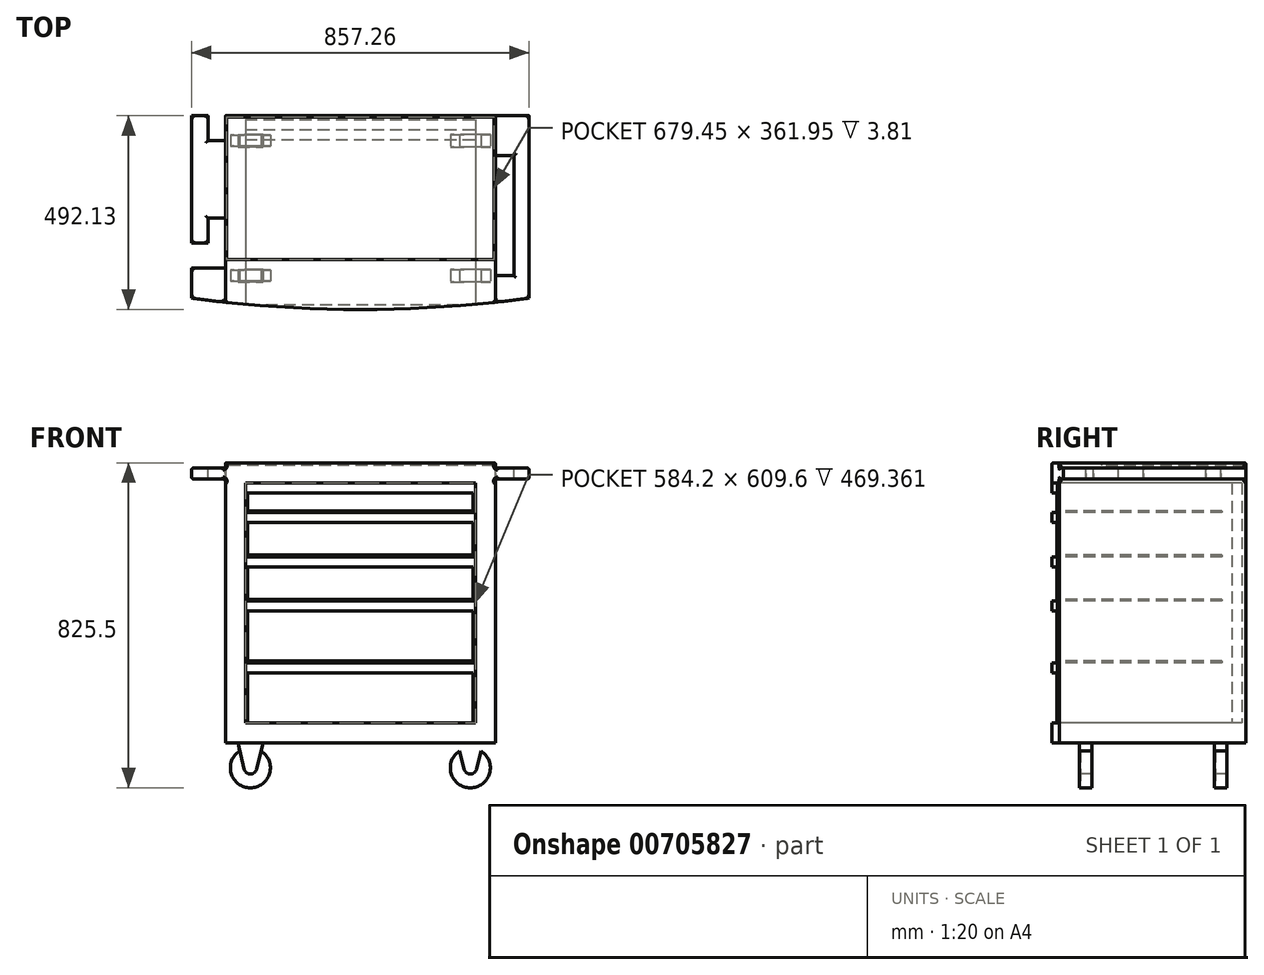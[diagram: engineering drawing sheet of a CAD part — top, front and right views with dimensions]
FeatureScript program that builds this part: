
annotation { "Feature Type Name" : "Feature", "Feature Type Description" : "" }
export const myFeature = defineFeature(function(context is Context, id is Id, definition is map)
    precondition{}
    {
        {
            var Q0;
            Q0=qCreatedBy(makeId("Front.planeOp"),FACE);
            var sketch = newSketch(context, id + "F0", { "sketchPlane" : qUnion([Q0])});
            skLineSegment(sketch, "E0", {"start": v(0, 0) * mm, "end": v(685.8, 0) * mm});
            skLineSegment(sketch, "E1", {"start": v(685.8, 0) * mm, "end": v(685.8, 669.92) * mm});
            skLineSegment(sketch, "E2", {"start": v(685.8, 669.93) * mm, "end": v(771.52, 669.93) * mm});
            skLineSegment(sketch, "E3", {"start": v(771.52, 669.93) * mm, "end": v(771.52, 711.2) * mm});
            skLineSegment(sketch, "E4", {"start": v(771.52, 711.2) * mm, "end": v(-85.72, 711.2) * mm});
            skLineSegment(sketch, "E5", {"start": v(-85.73, 711.2) * mm, "end": v(-85.73, 669.93) * mm});
            skLineSegment(sketch, "E6", {"start": v(-85.72, 669.93) * mm, "end": v(0, 669.93) * mm});
            skLineSegment(sketch, "E7", {"start": v(0, 669.92) * mm, "end": v(0, 0) * mm});
            skPoint(sketch, "E8", {"position": v(342.9, 711.2) * mm});
            skPoint(sketch, "E9", {"position": v(342.9, 0) * mm});
            skLineSegment(sketch, "E10.bottom", {"start": v(50.8, 660.4) * mm, "end": v(635, 660.4) * mm});
            skLineSegment(sketch, "E10.top", {"start": v(50.8, 50.8) * mm, "end": v(635, 50.8) * mm});
            skLineSegment(sketch, "E10.left", {"start": v(50.8, 660.4) * mm, "end": v(50.8, 50.8) * mm});
            skLineSegment(sketch, "E10.right", {"start": v(635, 660.4) * mm, "end": v(635, 50.8) * mm});
            skLineSegment(sketch, "E11", {"start": v(50.8, 203.2) * mm, "end": v(635, 203.2) * mm});
            skLineSegment(sketch, "E12", {"start": v(50.8, 360.04) * mm, "end": v(635, 360.05) * mm});
            skLineSegment(sketch, "E13", {"start": v(50.8, 472.44) * mm, "end": v(635, 472.44) * mm});
            skLineSegment(sketch, "E14", {"start": v(50.8, 584.83) * mm, "end": v(635, 584.84) * mm});
            skLineSegment(sketch, "E15", {"start": v(50.8, 207.64) * mm, "end": v(635, 207.65) * mm});
            skLineSegment(sketch, "E16", {"start": v(50.8, 364.49) * mm, "end": v(635, 364.5) * mm});
            skLineSegment(sketch, "E17", {"start": v(50.8, 476.88) * mm, "end": v(635, 476.89) * mm});
            skLineSegment(sketch, "E18", {"start": v(50.8, 589.28) * mm, "end": v(635, 589.28) * mm});
            skLineSegment(sketch, "E19", {"start": v(50.8, 635) * mm, "end": v(635, 635) * mm});
            skLineSegment(sketch, "E20", {"start": v(50.8, 559.43) * mm, "end": v(635, 559.44) * mm});
            skLineSegment(sketch, "E21", {"start": v(50.8, 447.04) * mm, "end": v(635, 447.04) * mm});
            skLineSegment(sketch, "E22", {"start": v(50.8, 334.64) * mm, "end": v(635, 334.65) * mm});
            skLineSegment(sketch, "E23", {"start": v(50.8, 177.8) * mm, "end": v(635, 177.8) * mm});
            skSolve(sketch);
        }
        {
            var Q0;
            Q0=makeQuery(id+"F0.imprint","IMPRINT",FACE,{"disambiguationData":[TD([[makeQuery(id+"F0.imprint","IMPRINT",EDGE,{"derivedFrom":sQuery(id+"F0.wireOp",EDGE,"E0")}),1.0]])]});
            var Q1;
            {var subQ0=sQuery(id+"F0.wireOp",EDGE,"E10.top");Q1=makeQuery(id+"F0.imprint","IMPRINT",FACE,{"disambiguationData":[TD([[makeQuery(id+"F0.imprint","IMPRINT",EDGE,{"derivedFrom":subQ0}),1.0]])]});}
            var Q2;
            {var subQ0=sQuery(id+"F0.wireOp",EDGE,"E11");Q2=makeQuery(id+"F0.imprint","IMPRINT",FACE,{"disambiguationData":[TD([[makeQuery(id+"F0.imprint","IMPRINT",EDGE,{"derivedFrom":subQ0}),-1.0]])]});}
            var Q3;
            {var subQ0=sQuery(id+"F0.wireOp",EDGE,"E11");Q3=makeQuery(id+"F0.imprint","IMPRINT",FACE,{"disambiguationData":[TD([[makeQuery(id+"F0.imprint","IMPRINT",EDGE,{"derivedFrom":subQ0}),1.0]])]});}
            var Q4;
            {var subQ0=sQuery(id+"F0.wireOp",EDGE,"E15");Q4=makeQuery(id+"F0.imprint","IMPRINT",FACE,{"disambiguationData":[TD([[makeQuery(id+"F0.imprint","IMPRINT",EDGE,{"derivedFrom":subQ0}),1.0]])]});}
            var Q5;
            {var subQ0=sQuery(id+"F0.wireOp",EDGE,"E12");Q5=makeQuery(id+"F0.imprint","IMPRINT",FACE,{"disambiguationData":[TD([[makeQuery(id+"F0.imprint","IMPRINT",EDGE,{"derivedFrom":subQ0}),-1.0]])]});}
            var Q6;
            {var subQ0=sQuery(id+"F0.wireOp",EDGE,"E12");Q6=makeQuery(id+"F0.imprint","IMPRINT",FACE,{"disambiguationData":[TD([[makeQuery(id+"F0.imprint","IMPRINT",EDGE,{"derivedFrom":subQ0}),1.0]])]});}
            var Q7;
            {var subQ0=sQuery(id+"F0.wireOp",EDGE,"E16");Q7=makeQuery(id+"F0.imprint","IMPRINT",FACE,{"disambiguationData":[TD([[makeQuery(id+"F0.imprint","IMPRINT",EDGE,{"derivedFrom":subQ0}),1.0]])]});}
            var Q8;
            {var subQ0=sQuery(id+"F0.wireOp",EDGE,"E13");Q8=makeQuery(id+"F0.imprint","IMPRINT",FACE,{"disambiguationData":[TD([[makeQuery(id+"F0.imprint","IMPRINT",EDGE,{"derivedFrom":subQ0}),-1.0]])]});}
            var Q9;
            {var subQ0=sQuery(id+"F0.wireOp",EDGE,"E13");Q9=makeQuery(id+"F0.imprint","IMPRINT",FACE,{"disambiguationData":[TD([[makeQuery(id+"F0.imprint","IMPRINT",EDGE,{"derivedFrom":subQ0}),1.0]])]});}
            var Q10;
            {var subQ0=sQuery(id+"F0.wireOp",EDGE,"E17");Q10=makeQuery(id+"F0.imprint","IMPRINT",FACE,{"disambiguationData":[TD([[makeQuery(id+"F0.imprint","IMPRINT",EDGE,{"derivedFrom":subQ0}),1.0]])]});}
            var Q11;
            {var subQ0=sQuery(id+"F0.wireOp",EDGE,"E14");Q11=makeQuery(id+"F0.imprint","IMPRINT",FACE,{"disambiguationData":[TD([[makeQuery(id+"F0.imprint","IMPRINT",EDGE,{"derivedFrom":subQ0}),-1.0]])]});}
            var Q12;
            {var subQ0=sQuery(id+"F0.wireOp",EDGE,"E14");Q12=makeQuery(id+"F0.imprint","IMPRINT",FACE,{"disambiguationData":[TD([[makeQuery(id+"F0.imprint","IMPRINT",EDGE,{"derivedFrom":subQ0}),1.0]])]});}
            var Q13;
            {var subQ0=sQuery(id+"F0.wireOp",EDGE,"E18");Q13=makeQuery(id+"F0.imprint","IMPRINT",FACE,{"disambiguationData":[TD([[makeQuery(id+"F0.imprint","IMPRINT",EDGE,{"derivedFrom":subQ0}),1.0]])]});}
            var Q14;
            {var subQ0=sQuery(id+"F0.wireOp",EDGE,"E10.bottom");Q14=makeQuery(id+"F0.imprint","IMPRINT",FACE,{"disambiguationData":[TD([[makeQuery(id+"F0.imprint","IMPRINT",EDGE,{"derivedFrom":subQ0}),-1.0]])]});}
            extrude(context, id + "F1", {"entities" : qUnion([Q0, Q1, Q2, Q3, Q4, Q5, Q6, Q7, Q8, Q9, Q10, Q11, Q12, Q13, Q14]), "oppositeDirection" : true, "depth" : 492.12 * mm, "offsetDistance" : 25.4 * mm});
        }
        {
            var Q0;
            {var subQ0=sQuery(id+"F0.wireOp",EDGE,"E10.bottom");Q0=makeQuery(id+"F0.imprint","IMPRINT",FACE,{"disambiguationData":[TD([[makeQuery(id+"F0.imprint","IMPRINT",EDGE,{"derivedFrom":subQ0}),-1.0]])]});}
            var Q1;
            {var subQ0=sQuery(id+"F0.wireOp",EDGE,"E18");Q1=makeQuery(id+"F0.imprint","IMPRINT",FACE,{"disambiguationData":[TD([[makeQuery(id+"F0.imprint","IMPRINT",EDGE,{"derivedFrom":subQ0}),1.0]])]});}
            var Q2;
            {var subQ0=sQuery(id+"F0.wireOp",EDGE,"E14");Q2=makeQuery(id+"F0.imprint","IMPRINT",FACE,{"disambiguationData":[TD([[makeQuery(id+"F0.imprint","IMPRINT",EDGE,{"derivedFrom":subQ0}),1.0]])]});}
            var Q3;
            {var subQ0=sQuery(id+"F0.wireOp",EDGE,"E14");Q3=makeQuery(id+"F0.imprint","IMPRINT",FACE,{"disambiguationData":[TD([[makeQuery(id+"F0.imprint","IMPRINT",EDGE,{"derivedFrom":subQ0}),-1.0]])]});}
            var Q4;
            {var subQ0=sQuery(id+"F0.wireOp",EDGE,"E17");Q4=makeQuery(id+"F0.imprint","IMPRINT",FACE,{"disambiguationData":[TD([[makeQuery(id+"F0.imprint","IMPRINT",EDGE,{"derivedFrom":subQ0}),1.0]])]});}
            var Q5;
            {var subQ0=sQuery(id+"F0.wireOp",EDGE,"E13");Q5=makeQuery(id+"F0.imprint","IMPRINT",FACE,{"disambiguationData":[TD([[makeQuery(id+"F0.imprint","IMPRINT",EDGE,{"derivedFrom":subQ0}),1.0]])]});}
            var Q6;
            {var subQ0=sQuery(id+"F0.wireOp",EDGE,"E13");Q6=makeQuery(id+"F0.imprint","IMPRINT",FACE,{"disambiguationData":[TD([[makeQuery(id+"F0.imprint","IMPRINT",EDGE,{"derivedFrom":subQ0}),-1.0]])]});}
            var Q7;
            {var subQ0=sQuery(id+"F0.wireOp",EDGE,"E16");Q7=makeQuery(id+"F0.imprint","IMPRINT",FACE,{"disambiguationData":[TD([[makeQuery(id+"F0.imprint","IMPRINT",EDGE,{"derivedFrom":subQ0}),1.0]])]});}
            var Q8;
            {var subQ0=sQuery(id+"F0.wireOp",EDGE,"E12");Q8=makeQuery(id+"F0.imprint","IMPRINT",FACE,{"disambiguationData":[TD([[makeQuery(id+"F0.imprint","IMPRINT",EDGE,{"derivedFrom":subQ0}),1.0]])]});}
            var Q9;
            {var subQ0=sQuery(id+"F0.wireOp",EDGE,"E12");Q9=makeQuery(id+"F0.imprint","IMPRINT",FACE,{"disambiguationData":[TD([[makeQuery(id+"F0.imprint","IMPRINT",EDGE,{"derivedFrom":subQ0}),-1.0]])]});}
            var Q10;
            {var subQ0=sQuery(id+"F0.wireOp",EDGE,"E15");Q10=makeQuery(id+"F0.imprint","IMPRINT",FACE,{"disambiguationData":[TD([[makeQuery(id+"F0.imprint","IMPRINT",EDGE,{"derivedFrom":subQ0}),1.0]])]});}
            var Q11;
            {var subQ0=sQuery(id+"F0.wireOp",EDGE,"E11");Q11=makeQuery(id+"F0.imprint","IMPRINT",FACE,{"disambiguationData":[TD([[makeQuery(id+"F0.imprint","IMPRINT",EDGE,{"derivedFrom":subQ0}),1.0]])]});}
            var Q12;
            {var subQ0=sQuery(id+"F0.wireOp",EDGE,"E11");Q12=makeQuery(id+"F0.imprint","IMPRINT",FACE,{"disambiguationData":[TD([[makeQuery(id+"F0.imprint","IMPRINT",EDGE,{"derivedFrom":subQ0}),-1.0]])]});}
            var Q13;
            {var subQ0=sQuery(id+"F0.wireOp",EDGE,"E10.top");Q13=makeQuery(id+"F0.imprint","IMPRINT",FACE,{"disambiguationData":[TD([[makeQuery(id+"F0.imprint","IMPRINT",EDGE,{"derivedFrom":subQ0}),1.0]])]});}
            extrude(context, id + "F2", {"entities" : qUnion([Q0, Q1, Q2, Q3, Q4, Q5, Q6, Q7, Q8, Q9, Q10, Q11, Q12, Q13]), "operationType" : NewBodyOperationType.REMOVE, "oppositeDirection" : true, "depth" : 482.6 * mm, "offsetDistance" : 25.4 * mm});
        }
        {
            var Q0;
            {var subQ0=sQuery(id+"F0.wireOp",EDGE,"E10.bottom");Q0=makeQuery(id+"F0.imprint","IMPRINT",FACE,{"disambiguationData":[TD([[makeQuery(id+"F0.imprint","IMPRINT",EDGE,{"derivedFrom":subQ0}),-1.0]])]});}
            var Q1;
            {var subQ0=sQuery(id+"F0.wireOp",EDGE,"E18");Q1=makeQuery(id+"F0.imprint","IMPRINT",FACE,{"disambiguationData":[TD([[makeQuery(id+"F0.imprint","IMPRINT",EDGE,{"derivedFrom":subQ0}),1.0]])]});}
            var Q2;
            {var subQ0=sQuery(id+"F0.wireOp",EDGE,"E14");Q2=makeQuery(id+"F0.imprint","IMPRINT",FACE,{"disambiguationData":[TD([[makeQuery(id+"F0.imprint","IMPRINT",EDGE,{"derivedFrom":subQ0}),-1.0]])]});}
            var Q3;
            {var subQ0=sQuery(id+"F0.wireOp",EDGE,"E17");Q3=makeQuery(id+"F0.imprint","IMPRINT",FACE,{"disambiguationData":[TD([[makeQuery(id+"F0.imprint","IMPRINT",EDGE,{"derivedFrom":subQ0}),1.0]])]});}
            var Q4;
            {var subQ0=sQuery(id+"F0.wireOp",EDGE,"E13");Q4=makeQuery(id+"F0.imprint","IMPRINT",FACE,{"disambiguationData":[TD([[makeQuery(id+"F0.imprint","IMPRINT",EDGE,{"derivedFrom":subQ0}),-1.0]])]});}
            var Q5;
            {var subQ0=sQuery(id+"F0.wireOp",EDGE,"E16");Q5=makeQuery(id+"F0.imprint","IMPRINT",FACE,{"disambiguationData":[TD([[makeQuery(id+"F0.imprint","IMPRINT",EDGE,{"derivedFrom":subQ0}),1.0]])]});}
            var Q6;
            {var subQ0=sQuery(id+"F0.wireOp",EDGE,"E12");Q6=makeQuery(id+"F0.imprint","IMPRINT",FACE,{"disambiguationData":[TD([[makeQuery(id+"F0.imprint","IMPRINT",EDGE,{"derivedFrom":subQ0}),-1.0]])]});}
            var Q7;
            {var subQ0=sQuery(id+"F0.wireOp",EDGE,"E15");Q7=makeQuery(id+"F0.imprint","IMPRINT",FACE,{"disambiguationData":[TD([[makeQuery(id+"F0.imprint","IMPRINT",EDGE,{"derivedFrom":subQ0}),1.0]])]});}
            var Q8;
            {var subQ0=sQuery(id+"F0.wireOp",EDGE,"E11");Q8=makeQuery(id+"F0.imprint","IMPRINT",FACE,{"disambiguationData":[TD([[makeQuery(id+"F0.imprint","IMPRINT",EDGE,{"derivedFrom":subQ0}),-1.0]])]});}
            var Q9;
            {var subQ0=sQuery(id+"F0.wireOp",EDGE,"E10.top");Q9=makeQuery(id+"F0.imprint","IMPRINT",FACE,{"disambiguationData":[TD([[makeQuery(id+"F0.imprint","IMPRINT",EDGE,{"derivedFrom":subQ0}),1.0]])]});}
            var Q10;
            {var subQ0=sQuery(id+"F0.wireOp",EDGE,"E11");Q10=makeQuery(id+"F0.imprint","IMPRINT",FACE,{"disambiguationData":[TD([[makeQuery(id+"F0.imprint","IMPRINT",EDGE,{"derivedFrom":subQ0}),1.0]])]});}
            var Q11;
            {var subQ0=sQuery(id+"F0.wireOp",EDGE,"E12");Q11=makeQuery(id+"F0.imprint","IMPRINT",FACE,{"disambiguationData":[TD([[makeQuery(id+"F0.imprint","IMPRINT",EDGE,{"derivedFrom":subQ0}),1.0]])]});}
            var Q12;
            {var subQ0=sQuery(id+"F0.wireOp",EDGE,"E13");Q12=makeQuery(id+"F0.imprint","IMPRINT",FACE,{"disambiguationData":[TD([[makeQuery(id+"F0.imprint","IMPRINT",EDGE,{"derivedFrom":subQ0}),1.0]])]});}
            var Q13;
            {var subQ0=sQuery(id+"F0.wireOp",EDGE,"E14");Q13=makeQuery(id+"F0.imprint","IMPRINT",FACE,{"disambiguationData":[TD([[makeQuery(id+"F0.imprint","IMPRINT",EDGE,{"derivedFrom":subQ0}),1.0]])]});}
            extrude(context, id + "F3", {"entities" : qUnion([Q0, Q1, Q2, Q3, Q4, Q5, Q6, Q7, Q8, Q9, Q10, Q11, Q12, Q13]), "oppositeDirection" : true, "depth" : 457.2 * mm, "offsetDistance" : 25.4 * mm});
        }
        {
            var Q0;
            {var subQ0=sQuery(id+"F0.wireOp",EDGE,"E18");Q0=makeQuery(id+"F0.imprint","IMPRINT",FACE,{"disambiguationData":[TD([[makeQuery(id+"F0.imprint","IMPRINT",EDGE,{"derivedFrom":subQ0}),1.0]])]});}
            var Q1;
            {var subQ0=sQuery(id+"F0.wireOp",EDGE,"E17");Q1=makeQuery(id+"F0.imprint","IMPRINT",FACE,{"disambiguationData":[TD([[makeQuery(id+"F0.imprint","IMPRINT",EDGE,{"derivedFrom":subQ0}),1.0]])]});}
            var Q2;
            {var subQ0=sQuery(id+"F0.wireOp",EDGE,"E16");Q2=makeQuery(id+"F0.imprint","IMPRINT",FACE,{"disambiguationData":[TD([[makeQuery(id+"F0.imprint","IMPRINT",EDGE,{"derivedFrom":subQ0}),1.0]])]});}
            var Q3;
            {var subQ0=sQuery(id+"F0.wireOp",EDGE,"E15");Q3=makeQuery(id+"F0.imprint","IMPRINT",FACE,{"disambiguationData":[TD([[makeQuery(id+"F0.imprint","IMPRINT",EDGE,{"derivedFrom":subQ0}),1.0]])]});}
            var Q4;
            {var subQ0=sQuery(id+"F0.wireOp",EDGE,"E10.top");Q4=makeQuery(id+"F0.imprint","IMPRINT",FACE,{"disambiguationData":[TD([[makeQuery(id+"F0.imprint","IMPRINT",EDGE,{"derivedFrom":subQ0}),1.0]])]});}
            extrude(context, id + "F4", {"entities" : qUnion([Q0, Q1, Q2, Q3, Q4]), "operationType" : NewBodyOperationType.REMOVE, "oppositeDirection" : true, "depth" : 12.7 * mm, "offsetDistance" : 25.4 * mm});
        }
        {
            var Q0;
            {var subQ0=sQuery(id+"F0.wireOp",EDGE,"E14");Q0=makeQuery(id+"F0.imprint","IMPRINT",FACE,{"disambiguationData":[TD([[makeQuery(id+"F0.imprint","IMPRINT",EDGE,{"derivedFrom":subQ0}),1.0]])]});}
            var Q1;
            {var subQ0=sQuery(id+"F0.wireOp",EDGE,"E13");Q1=makeQuery(id+"F0.imprint","IMPRINT",FACE,{"disambiguationData":[TD([[makeQuery(id+"F0.imprint","IMPRINT",EDGE,{"derivedFrom":subQ0}),1.0]])]});}
            var Q2;
            {var subQ0=sQuery(id+"F0.wireOp",EDGE,"E12");Q2=makeQuery(id+"F0.imprint","IMPRINT",FACE,{"disambiguationData":[TD([[makeQuery(id+"F0.imprint","IMPRINT",EDGE,{"derivedFrom":subQ0}),1.0]])]});}
            var Q3;
            {var subQ0=sQuery(id+"F0.wireOp",EDGE,"E11");Q3=makeQuery(id+"F0.imprint","IMPRINT",FACE,{"disambiguationData":[TD([[makeQuery(id+"F0.imprint","IMPRINT",EDGE,{"derivedFrom":subQ0}),1.0]])]});}
            extrude(context, id + "F5", {"entities" : qUnion([Q0, Q1, Q2, Q3]), "operationType" : NewBodyOperationType.REMOVE, "oppositeDirection" : true, "depth" : 431.8 * mm, "offsetDistance" : 25.4 * mm});
        }
        {
            var Q0;
            Q0=makeQuery(id+"F1.opExtrude","CAP_FACE",FACE,{"disambiguationData":[OSD([sQuery(id+"F0.wireOp",EDGE,"E0"),sQuery(id+"F0.wireOp",EDGE,"E1"),sQuery(id+"F0.wireOp",EDGE,"E2"),sQuery(id+"F0.wireOp",EDGE,"E3"),sQuery(id+"F0.wireOp",EDGE,"E4"),sQuery(id+"F0.wireOp",EDGE,"E5"),sQuery(id+"F0.wireOp",EDGE,"E6"),sQuery(id+"F0.wireOp",EDGE,"E7")])],"isStart":false});
            cPlane(context, id + "F6", {"entities" : qUnion([Q0]), "cplaneType" : CPlaneType.OFFSET, "offset" : 63.5 * mm, "oppositeDirection" : true, "width" : 152.4 * mm, "height" : 152.4 * mm});
        }
        {
            var Q0;
            Q0=qCreatedBy(id+"F6.planeOp",FACE);
            var sketch = newSketch(context, id + "F7", { "sketchPlane" : qUnion([Q0])});
            skLineSegment(sketch, "E24.0", {"start": v(0, 0) * mm, "end": v(-685.8, 0) * mm});
            skLineSegment(sketch, "E25", {"start": v(-63.5, -63.5) * mm, "end": v(-63.5, 0) * mm, "construction": true});
            skLineSegment(sketch, "E26", {"start": v(-31.75, 0) * mm, "end": v(-95.25, 0) * mm});
            skPoint(sketch, "E27", {"position": v(-63.5, 0) * mm});
            skLineSegment(sketch, "E28", {"start": v(-31.75, 0) * mm, "end": v(-48.07, -67.24) * mm});
            skLineSegment(sketch, "E29.MirrorCS", {"start": v(-95.25, 0) * mm, "end": v(-78.93, -67.24) * mm});
            skArc(sketch, "E30", {"start": v(-36.69, -20.35) * mm, "mid": v(-63.5, -12.7) * mm, "end": v(-90.31, -20.35) * mm, "construction": true});
            skArc(sketch, "E31", {"start": v(-90.31, -20.35) * mm, "mid": v(-63.5, -114.3) * mm, "end": v(-36.69, -20.35) * mm});
            skArc(sketch, "E32", {"start": v(-48.07, -67.24) * mm, "mid": v(-63.5, -47.62) * mm, "end": v(-78.93, -67.24) * mm, "construction": true});
            skArc(sketch, "E33", {"start": v(-78.93, -67.24) * mm, "mid": v(-63.5, -79.38) * mm, "end": v(-48.07, -67.24) * mm});
            skLineSegment(sketch, "E34", {"start": v(-342.9, 0) * mm, "end": v(-342.9, -115.86) * mm, "construction": true});
            skArc(sketch, "E35.MirrorCS", {"start": v(-595.49, -20.35) * mm, "mid": v(-622.3, -114.3) * mm, "end": v(-649.11, -20.35) * mm});
            skArc(sketch, "E36.MirrorCS", {"start": v(-606.87, -67.24) * mm, "mid": v(-622.3, -79.38) * mm, "end": v(-637.73, -67.24) * mm});
            skLineSegment(sketch, "E37.MirrorCS", {"start": v(-590.55, 0) * mm, "end": v(-606.87, -67.24) * mm});
            skLineSegment(sketch, "E38.MirrorCS", {"start": v(-654.05, 0) * mm, "end": v(-637.73, -67.24) * mm});
            skSolve(sketch);
        }
        {
            var Q0;
            {var subQ3=sQuery(id+"F7.wireOp",EDGE,"E33");Q0=makeQuery(id+"F7.imprint","IMPRINT",FACE,{"disambiguationData":[TD([[makeQuery(id+"F7.imprint","IMPRINT",EDGE,{"derivedFrom":subQ3}),1.0]])]});}
            var Q1;
            {var subQ3=sQuery(id+"F7.wireOp",EDGE,"E36.MirrorCS");Q1=makeQuery(id+"F7.imprint","IMPRINT",FACE,{"disambiguationData":[TD([[makeQuery(id+"F7.imprint","IMPRINT",EDGE,{"derivedFrom":subQ3}),-1.0]])]});}
            extrude(context, id + "F8", {"entities" : qUnion([Q0, Q1]), "operationType" : NewBodyOperationType.ADD, "depth" : 31.75 * mm, "offsetDistance" : 25.4 * mm, "symmetric" : true});
        }
        {
            var Q0;
            {var subQ0=sQuery(id+"F7.wireOp",EDGE,"E31");Q0=makeQuery(id+"F7.imprint","IMPRINT",FACE,{"disambiguationData":[TD([[makeQuery(id+"F7.imprint","IMPRINT",EDGE,{"derivedFrom":subQ0}),1.0]])]});}
            var Q1;
            {var subQ0=sQuery(id+"F7.wireOp",EDGE,"E35.MirrorCS");Q1=makeQuery(id+"F7.imprint","IMPRINT",FACE,{"disambiguationData":[TD([[makeQuery(id+"F7.imprint","IMPRINT",EDGE,{"derivedFrom":subQ0}),-1.0]])]});}
            extrude(context, id + "F9", {"entities" : qUnion([Q0, Q1]), "operationType" : NewBodyOperationType.ADD, "depth" : 28.57 * mm, "offsetDistance" : 25.4 * mm, "symmetric" : true});
        }
        {
            var Q0;
            Q0=makeQuery(id+"F1.opExtrude","CAP_FACE",FACE,{"disambiguationData":[OSD([sQuery(id+"F0.wireOp",EDGE,"E0"),sQuery(id+"F0.wireOp",EDGE,"E1"),sQuery(id+"F0.wireOp",EDGE,"E2"),sQuery(id+"F0.wireOp",EDGE,"E3"),sQuery(id+"F0.wireOp",EDGE,"E4"),sQuery(id+"F0.wireOp",EDGE,"E5"),sQuery(id+"F0.wireOp",EDGE,"E6"),sQuery(id+"F0.wireOp",EDGE,"E7")])],"isStart":false});
            cPlane(context, id + "F10", {"entities" : qUnion([Q0]), "cplaneType" : CPlaneType.OFFSET, "offset" : 406.4 * mm, "oppositeDirection" : true, "width" : 152.4 * mm, "height" : 152.4 * mm});
        }
        {
            var Q0;
            Q0=qCreatedBy(id+"F10.planeOp",FACE);
            var sketch = newSketch(context, id + "F11", { "sketchPlane" : qUnion([Q0])});
            skArc(sketch, "E39.0", {"start": v(-90.31, -20.35) * mm, "mid": v(-63.5, -114.3) * mm, "end": v(-36.69, -20.35) * mm});
            skArc(sketch, "E40.0", {"start": v(-78.93, -67.24) * mm, "mid": v(-63.5, -79.38) * mm, "end": v(-48.07, -67.24) * mm});
            skLineSegment(sketch, "E41.0", {"start": v(-31.75, 0) * mm, "end": v(-48.07, -67.24) * mm});
            skLineSegment(sketch, "E42.0", {"start": v(-95.25, 0) * mm, "end": v(-78.93, -67.24) * mm});
            skLineSegment(sketch, "E43.0", {"start": v(0, 0) * mm, "end": v(-685.8, 0) * mm});
            skArc(sketch, "E44.0", {"start": v(-595.49, -20.35) * mm, "mid": v(-622.3, -114.3) * mm, "end": v(-649.11, -20.35) * mm});
            skArc(sketch, "E45.0", {"start": v(-606.87, -67.24) * mm, "mid": v(-622.3, -79.38) * mm, "end": v(-637.73, -67.24) * mm});
            skLineSegment(sketch, "E46.0", {"start": v(-590.55, 0) * mm, "end": v(-606.87, -67.24) * mm});
            skLineSegment(sketch, "E47.0", {"start": v(-654.05, 0) * mm, "end": v(-637.73, -67.24) * mm});
            skSolve(sketch);
        }
        {
            var Q0;
            {var subQ7=sQuery(id+"F11.wireOp",EDGE,"E40.0");Q0=makeQuery(id+"F11.imprint","IMPRINT",FACE,{"disambiguationData":[TD([[makeQuery(id+"F11.imprint","IMPRINT",EDGE,{"derivedFrom":subQ7}),1.0]])]});}
            var Q1;
            {var subQ3=sQuery(id+"F11.wireOp",EDGE,"E45.0");Q1=makeQuery(id+"F11.imprint","IMPRINT",FACE,{"disambiguationData":[TD([[makeQuery(id+"F11.imprint","IMPRINT",EDGE,{"derivedFrom":subQ3}),-1.0]])]});}
            extrude(context, id + "F12", {"entities" : qUnion([Q0, Q1]), "operationType" : NewBodyOperationType.ADD, "depth" : 31.75 * mm, "offsetDistance" : 25.4 * mm, "symmetric" : true});
        }
        {
            var Q0;
            {var subQ0=sQuery(id+"F11.wireOp",EDGE,"E39.0");Q0=makeQuery(id+"F11.imprint","IMPRINT",FACE,{"disambiguationData":[TD([[makeQuery(id+"F11.imprint","IMPRINT",EDGE,{"derivedFrom":subQ0}),1.0]])]});}
            var Q1;
            {var subQ0=sQuery(id+"F11.wireOp",EDGE,"E44.0");Q1=makeQuery(id+"F11.imprint","IMPRINT",FACE,{"disambiguationData":[TD([[makeQuery(id+"F11.imprint","IMPRINT",EDGE,{"derivedFrom":subQ0}),-1.0]])]});}
            extrude(context, id + "F13", {"entities" : qUnion([Q0, Q1]), "operationType" : NewBodyOperationType.ADD, "depth" : 28.57 * mm, "offsetDistance" : 25.4 * mm, "symmetric" : true});
        }
        {
            var Q0;
            Q0=makeQuery(id+"F1.opExtrude","SWEPT_FACE",FACE,{"disambiguationData":[OSD([sQuery(id+"F0.wireOp",EDGE,"E4")])]});
            var sketch = newSketch(context, id + "F14", { "sketchPlane" : qUnion([Q0])});
            skLineSegment(sketch, "E48.0.0", {"start": v(-85.72, 0) * mm, "end": v(771.52, 0) * mm});
            skLineSegment(sketch, "E48.0.1", {"start": v(771.52, 0) * mm, "end": v(771.52, 492.13) * mm});
            skLineSegment(sketch, "E48.0.2", {"start": v(771.52, 492.13) * mm, "end": v(-85.72, 492.13) * mm});
            skLineSegment(sketch, "E48.0.3", {"start": v(-85.73, 492.13) * mm, "end": v(-85.73, 0) * mm});
            skLineSegment(sketch, "E49", {"start": v(-85.72, 28.57) * mm, "end": v(771.52, 28.58) * mm, "construction": true});
            skPoint(sketch, "E50", {"position": v(342.9, 28.58) * mm});
            skLineSegment(sketch, "E51", {"start": v(342.9, 28.58) * mm, "end": v(342.9, 0) * mm, "construction": true});
            skArc(sketch, "E52", {"start": v(-85.72, 28.58) * mm, "mid": v(342.9, 0) * mm, "end": v(771.52, 28.58) * mm});
            skLineSegment(sketch, "E53", {"start": v(342.9, 28.58) * mm, "end": v(342.9, 492.13) * mm, "construction": true});
            skPoint(sketch, "E54.0", {"position": v(0, 0) * mm});
            skPoint(sketch, "E55.0", {"position": v(685.8, 0) * mm});
            skLineSegment(sketch, "E56", {"start": v(0, 0) * mm, "end": v(0, 492.13) * mm});
            skLineSegment(sketch, "E57", {"start": v(685.8, 0) * mm, "end": v(685.8, 492.13) * mm});
            skLineSegment(sketch, "E58", {"start": v(-85.72, 104.77) * mm, "end": v(0, 104.77) * mm});
            skLineSegment(sketch, "E59", {"start": v(0, 231.77) * mm, "end": v(-44.45, 231.77) * mm});
            skLineSegment(sketch, "E60", {"start": v(-44.45, 231.77) * mm, "end": v(-44.45, 168.27) * mm});
            skLineSegment(sketch, "E61", {"start": v(-44.45, 168.27) * mm, "end": v(-85.72, 168.27) * mm});
            skLineSegment(sketch, "E62", {"start": v(-44.45, 492.13) * mm, "end": v(-44.45, 428.63) * mm});
            skLineSegment(sketch, "E63", {"start": v(-44.45, 428.63) * mm, "end": v(0, 428.63) * mm});
            skLineSegment(sketch, "E64", {"start": v(685.8, 85.73) * mm, "end": v(733.42, 85.73) * mm});
            skLineSegment(sketch, "E65", {"start": v(733.42, 85.73) * mm, "end": v(733.42, 390.53) * mm});
            skLineSegment(sketch, "E66", {"start": v(733.42, 390.53) * mm, "end": v(685.8, 390.53) * mm});
            skLineSegment(sketch, "E67", {"start": v(3.17, 488.95) * mm, "end": v(3.18, 127) * mm});
            skLineSegment(sketch, "E68", {"start": v(3.18, 127) * mm, "end": v(682.62, 127) * mm});
            skLineSegment(sketch, "E69", {"start": v(682.62, 127) * mm, "end": v(682.62, 488.95) * mm});
            skLineSegment(sketch, "E70", {"start": v(682.62, 488.95) * mm, "end": v(3.17, 488.95) * mm});
            skSolve(sketch);
        }
        {
            var Q0;
            {var subQ3=sQuery(id+"F14.wireOp",EDGE,"E62");Q0=makeQuery(id+"F14.imprint","IMPRINT",FACE,{"disambiguationData":[TD([[makeQuery(id+"F14.imprint","IMPRINT",EDGE,{"derivedFrom":subQ3}),1.0]])]});}
            var Q1;
            {var subQ1=sQuery(id+"F14.wireOp",EDGE,"E58");Q1=makeQuery(id+"F14.imprint","IMPRINT",FACE,{"disambiguationData":[TD([[makeQuery(id+"F14.imprint","IMPRINT",EDGE,{"derivedFrom":subQ1}),1.0]])]});}
            var Q2;
            {var subQ0=sQuery(id+"F14.wireOp",EDGE,"E48.0.3");var subQ1=sQuery(id+"F14.wireOp",EDGE,"E48.0.0");var subQ2=makeQuery(id+"F14.imprint","INTERSECT",VERTEX,{"derivedFrom":[subQ1,subQ0]});Q2=makeQuery(id+"F14.imprint","IMPRINT",FACE,{"disambiguationData":[TD([[makeQuery(id+"F14.imprint","IMPRINT",EDGE,{"disambiguationData":[TD([[subQ2,1.0]])],"derivedFrom":subQ1}),-1.0]])]});}
            var Q3;
            {var subQ0=sQuery(id+"F14.wireOp",EDGE,"E56");var subQ1=sQuery(id+"F14.wireOp",EDGE,"E48.0.0");var subQ2=makeQuery(id+"F14.imprint","INTERSECT",VERTEX,{"derivedFrom":[subQ1,subQ0]});Q3=makeQuery(id+"F14.imprint","IMPRINT",FACE,{"disambiguationData":[TD([[makeQuery(id+"F14.imprint","IMPRINT",EDGE,{"disambiguationData":[TD([[subQ2,1.0]])],"derivedFrom":subQ1}),-1.0]])]});}
            var Q4;
            {var subQ0=sQuery(id+"F14.wireOp",EDGE,"E57");var subQ1=sQuery(id+"F14.wireOp",EDGE,"E48.0.0");var subQ2=makeQuery(id+"F14.imprint","INTERSECT",VERTEX,{"derivedFrom":[subQ1,subQ0]});Q4=makeQuery(id+"F14.imprint","IMPRINT",FACE,{"disambiguationData":[TD([[makeQuery(id+"F14.imprint","IMPRINT",EDGE,{"disambiguationData":[TD([[subQ2,-1.0]])],"derivedFrom":subQ1}),-1.0]])]});}
            var Q5;
            {var subQ0=sQuery(id+"F14.wireOp",EDGE,"E48.0.1");var subQ1=sQuery(id+"F14.wireOp",EDGE,"E48.0.0");var subQ2=makeQuery(id+"F14.imprint","INTERSECT",VERTEX,{"derivedFrom":[subQ1,subQ0]});Q5=makeQuery(id+"F14.imprint","IMPRINT",FACE,{"disambiguationData":[TD([[makeQuery(id+"F14.imprint","IMPRINT",EDGE,{"disambiguationData":[TD([[subQ2,-1.0]])],"derivedFrom":subQ1}),-1.0]])]});}
            var Q6;
            {var subQ0=sQuery(id+"F14.wireOp",EDGE,"E64");Q6=makeQuery(id+"F14.imprint","IMPRINT",FACE,{"disambiguationData":[TD([[makeQuery(id+"F14.imprint","IMPRINT",EDGE,{"derivedFrom":subQ0}),1.0]])]});}
            var Q7;
            Q7=makeQuery(id+"F1.opExtrude","SWEPT_FACE",FACE,{"disambiguationData":[OSD([sQuery(id+"F0.wireOp",EDGE,"E0")])]});
            extrude(context, id + "F15", {"entities" : qUnion([Q0, Q1, Q2, Q3, Q4, Q5, Q6]), "operationType" : NewBodyOperationType.REMOVE, "endBound" : BoundingType.UP_TO_SURFACE, "oppositeDirection" : true, "depth" : 25.4 * mm, "endBoundEntityFace" : qUnion([Q7]), "offsetDistance" : 25.4 * mm});
        }
        {
            var Q0;
            Q0=makeQuery(id+"F14.imprint","IMPRINT",FACE,{"disambiguationData":[TD([[makeQuery(id+"F14.imprint","IMPRINT",EDGE,{"derivedFrom":sQuery(id+"F14.wireOp",EDGE,"E67")}),1.0]])]});
            extrude(context, id + "F16", {"entities" : qUnion([Q0]), "operationType" : NewBodyOperationType.REMOVE, "oppositeDirection" : true, "depth" : 6.35 * mm, "offsetDistance" : 25.4 * mm});
        }
        {
            var Q0;
            {var subQ0=sQuery(id+"F0.wireOp",EDGE,"E2");var subQ1=sQuery(id+"F0.wireOp",EDGE,"E1");var subQ3=sQuery(id+"F0.wireOp",EDGE,"E3");var subQ4=sQuery(id+"F0.wireOp",EDGE,"E0");var subQ5=sQuery(id+"F0.wireOp",EDGE,"E4");var subQ6=sQuery(id+"F0.wireOp",EDGE,"E7");Q0=makeQuery(id+"F15.boolean.opBoolean","SPLIT",FACE,{"disambiguationData":[TD([makeQuery(id+"F1.opExtrude","SWEPT_FACE",FACE,{"disambiguationData":[OSD([subQ4])]})])],"derivedFrom":makeQuery(id+"F1.opExtrude","CAP_FACE",FACE,{"disambiguationData":[OSD([subQ4,subQ1,subQ0,subQ3,subQ5,sQuery(id+"F0.wireOp",EDGE,"E5"),sQuery(id+"F0.wireOp",EDGE,"E6"),subQ6])],"isStart":false})});}
            var sketch = newSketch(context, id + "F17", { "sketchPlane" : qUnion([Q0])});
            skLineSegment(sketch, "E71.0.0", {"start": v(0, 0) * mm, "end": v(0, 711.2) * mm});
            skLineSegment(sketch, "E71.0.1", {"start": v(0, 711.2) * mm, "end": v(-771.52, 711.2) * mm});
            skLineSegment(sketch, "E71.0.2", {"start": v(-771.52, 711.2) * mm, "end": v(-771.52, 669.93) * mm});
            skLineSegment(sketch, "E71.0.3", {"start": v(-771.52, 669.93) * mm, "end": v(-685.8, 669.93) * mm});
            skLineSegment(sketch, "E71.0.4", {"start": v(-685.8, 669.92) * mm, "end": v(-685.8, 0) * mm});
            skLineSegment(sketch, "E71.0.5", {"start": v(-685.8, 0) * mm, "end": v(0, 0) * mm});
            skLineSegment(sketch, "E72.0", {"start": v(85.73, 711.2) * mm, "end": v(85.73, 669.93) * mm});
            skLineSegment(sketch, "E73", {"start": v(-685.8, 669.93) * mm, "end": v(-685.8, 711.2) * mm});
            skLineSegment(sketch, "E74", {"start": v(0, 711.2) * mm, "end": v(85.73, 711.2) * mm});
            skLineSegment(sketch, "E75", {"start": v(-771.52, 698.5) * mm, "end": v(85.73, 698.5) * mm});
            skSolve(sketch);
        }
        {
            var Q0;
            {var subQ0=sQuery(id+"F17.wireOp",EDGE,"E71.0.2");var subQ1=sQuery(id+"F17.wireOp",EDGE,"E71.0.1");var subQ2=makeQuery(id+"F17.imprint","INTERSECT",VERTEX,{"derivedFrom":[subQ1,subQ0]});Q0=makeQuery(id+"F17.imprint","IMPRINT",FACE,{"disambiguationData":[TD([[makeQuery(id+"F17.imprint","IMPRINT",EDGE,{"disambiguationData":[TD([[subQ2,-1.0]])],"derivedFrom":subQ1}),-1.0]])]});}
            var Q1;
            {var subQ0=sQuery(id+"F17.wireOp",EDGE,"E74");Q1=makeQuery(id+"F17.imprint","IMPRINT",FACE,{"disambiguationData":[TD([[makeQuery(id+"F17.imprint","IMPRINT",EDGE,{"derivedFrom":subQ0}),-1.0]])]});}
            extrude(context, id + "F18", {"entities" : qUnion([Q0, Q1]), "operationType" : NewBodyOperationType.REMOVE, "oppositeDirection" : true, "depth" : 572 * mm, "offsetDistance" : 25.4 * mm});
        }
        {
            var Q0;
            {var subQ2=sQuery(id+"F14.wireOp",EDGE,"E59");var subQ6=sQuery(id+"F17.wireOp",EDGE,"E75");Q0=makeQuery(id+"F18.boolean.opBoolean","COPY",FACE,{"disambiguationData":[TD([makeQuery(id+"F15.boolean.opBoolean","COPY",FACE,{"derivedFrom":makeQuery(id+"F15.opExtrude","SWEPT_FACE",FACE,{"disambiguationData":[OSD([subQ2])]})})])],"derivedFrom":makeQuery(id+"F18.opExtrude","SWEPT_FACE",FACE,{"disambiguationData":[OSD([subQ6]),TDD([makeQuery(id+"F17.imprint","IMPRINT",EDGE,{"disambiguationData":[TD([[makeQuery(id+"F17.imprint","INTERSECT",VERTEX,{"derivedFrom":[sQuery(id+"F17.wireOp",EDGE,"E72.0"),subQ6]}),1.0]])],"derivedFrom":subQ6})])]})});}
            var Q1;
            {var subQ2=sQuery(id+"F14.wireOp",EDGE,"E59");var subQ3=sQuery(id+"F0.wireOp",EDGE,"E6");Q1=makeQuery(id+"F15.boolean.opBoolean","SPLIT",FACE,{"disambiguationData":[TD([makeQuery(id+"F15.opExtrude","SWEPT_FACE",FACE,{"disambiguationData":[OSD([subQ2])]})])],"derivedFrom":makeQuery(id+"F1.opExtrude","SWEPT_FACE",FACE,{"disambiguationData":[OSD([subQ3])]})});}
            var Q2;
            {var subQ2=sQuery(id+"F14.wireOp",EDGE,"E58");var subQ7=sQuery(id+"F17.wireOp",EDGE,"E75");Q2=makeQuery(id+"F18.boolean.opBoolean","COPY",FACE,{"disambiguationData":[TD([makeQuery(id+"F15.boolean.opBoolean","COPY",FACE,{"derivedFrom":makeQuery(id+"F15.opExtrude","SWEPT_FACE",FACE,{"disambiguationData":[OSD([subQ2])]})})])],"derivedFrom":makeQuery(id+"F18.opExtrude","SWEPT_FACE",FACE,{"disambiguationData":[OSD([subQ7]),TDD([makeQuery(id+"F17.imprint","IMPRINT",EDGE,{"disambiguationData":[TD([[makeQuery(id+"F17.imprint","INTERSECT",VERTEX,{"derivedFrom":[sQuery(id+"F17.wireOp",EDGE,"E72.0"),subQ7]}),1.0]])],"derivedFrom":subQ7})])]})});}
            var Q3;
            {var subQ5=sQuery(id+"F14.wireOp",EDGE,"E58");Q3=makeQuery(id+"F15.boolean.opBoolean","SPLIT",FACE,{"disambiguationData":[TD([makeQuery(id+"F15.opExtrude","SWEPT_FACE",FACE,{"disambiguationData":[OSD([subQ5])]})])],"derivedFrom":makeQuery(id+"F1.opExtrude","SWEPT_FACE",FACE,{"disambiguationData":[OSD([sQuery(id+"F0.wireOp",EDGE,"E6")])]})});}
            var Q4;
            {var subQ0=sQuery(id+"F17.wireOp",EDGE,"E75");Q4=makeQuery(id+"F18.boolean.opBoolean","COPY",FACE,{"derivedFrom":makeQuery(id+"F18.opExtrude","SWEPT_FACE",FACE,{"disambiguationData":[OSD([subQ0]),TDD([makeQuery(id+"F17.imprint","IMPRINT",EDGE,{"disambiguationData":[TD([[makeQuery(id+"F17.imprint","INTERSECT",VERTEX,{"derivedFrom":[sQuery(id+"F17.wireOp",EDGE,"E71.0.2"),subQ0]}),-1.0]])],"derivedFrom":subQ0})])]})});}
            var Q5;
            Q5=makeQuery(id+"F1.opExtrude","SWEPT_FACE",FACE,{"disambiguationData":[OSD([sQuery(id+"F0.wireOp",EDGE,"E2")])]});
            fillet(context, id + "F19", {"entities" : qUnion([Q0, Q1, Q2, Q3, Q4, Q5]), "radius" : 5.08 * mm, "tangentPropagation" : true, "allowEdgeOverflow" : false});
        }
        {
            var Q0;
            Q0=makeQuery(id+"F1.opExtrude","SWEPT_FACE",FACE,{"disambiguationData":[OSD([sQuery(id+"F0.wireOp",EDGE,"E4")])]});
            fillet(context, id + "F20", {"entities" : qUnion([Q0]), "radius" : 2.54 * mm, "tangentPropagation" : true, "allowEdgeOverflow" : false});
        }
    });
